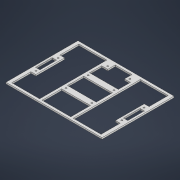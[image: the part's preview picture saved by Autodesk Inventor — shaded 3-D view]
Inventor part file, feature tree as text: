
AUTODESK INVENTOR PART (.ipt)
format: ipt  version: 2021 (Build 250183000, 183)  size: 404,992 bytes
history: native  units: mm
features: extrude x7, sketch x3
ambient origin geometry x8: Origin, YZ Plane, XZ Plane, XY Plane, X Axis, Y Axis, Z Axis, Center Point
bodies: Volumenkörper1 (feature_tree)
feature tree (10):
  extrude  "Extrusion1"  Depth=150.0mm
  sketch  "Skizze11"  dims[d2=3.0mm d3=0.0mm d50=3.2mm]
  extrude  "Extrusion12"  Depth=3.0mm
  extrude  "Extrusion13"  Depth=4.0mm
  extrude  "Extrusion14"  Depth=4.0mm
  extrude  "Extrusion15"  Depth=4.0mm
  extrude  "Extrusion16"  Depth=4.0mm
  extrude  "Extrusion17"  Depth=4.0mm TaperAngle=0.0deg
  sketch  "Skizze1"  dims[d0=200.0mm d1=150.0mm]
  sketch  "Skizze12"  dims[d51=3.2mm d52=23.0mm d53=23.0mm d54=73.0mm d55=73.0mm d56=17.5mm d57=0.0mm d60=10.0mm d61=0.0mm d62=3.2mm d63=3.2mm d64=27.0mm d65=27.0mm d66=52.0mm d67=52.0mm d68=10.0mm d69=0.0mm d70=3.2mm d71=3.2mm d72=23.0mm d73=23.0mm d74=10.5mm d75=10.5mm d76=3.2mm d77=3.2mm d78=10.5mm d79=10.5mm d80=23.0mm d81=23.0mm d82=10.0mm d83=0.0mm d84=3.2mm d85=3.2mm d86=23.0mm d87=23.0mm d88=15.0mm d89=15.0mm d90=10.0mm d91=0.0mm d92=10.0mm d93=0.0mm d94=5.0mm d95=7.0mm d96=5.0mm d97=65.0mm d98=7.0mm d99=65.0mm d100=40.0mm d101=25.0mm d102=21.0mm d103=5.0mm d104=5.0mm d105=5.0mm d106=5.0mm d107=10.0mm d108=60.0mm d109=17.0mm d110=7.0mm d111=10.0mm d112=60.0mm d113=17.0mm d114=7.0mm d115=5.0mm d116=12.0mm d117=17.0mm d118=12.0mm d119=5.0mm d120=5.0mm d121=4.0mm d122=4.0mm d123=4.0mm d124=4.0mm d126=5.6mm d127=4.0mm d128=4.0mm d129=4.0mm d130=4.0mm d131=4.0mm]
